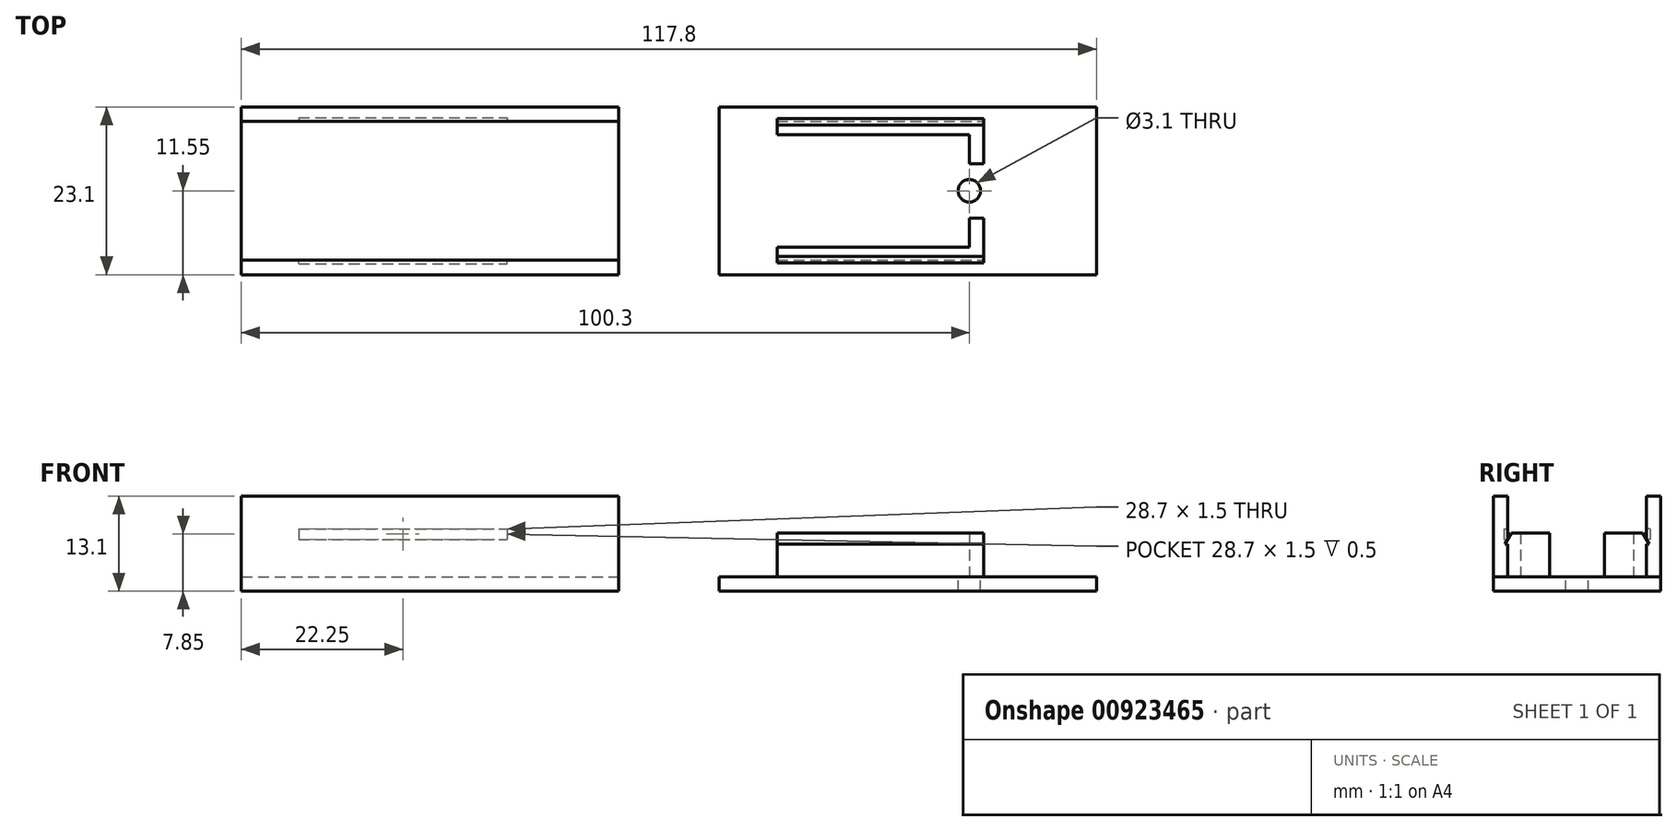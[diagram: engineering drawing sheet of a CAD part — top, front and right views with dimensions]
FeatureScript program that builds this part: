
annotation { "Feature Type Name" : "Feature", "Feature Type Description" : "" }
export const myFeature = defineFeature(function(context is Context, id is Id, definition is map)
    precondition{}
    {
        {
            var Q0;
            Q0=qCreatedBy(makeId("Top.planeOp"),FACE);
            var sketch = newSketch(context, id + "F0", { "sketchPlane" : qUnion([Q0])});
            skLineSegment(sketch, "E0.bottom", {"start": v(-26, 11.55) * mm, "end": v(26, 11.55) * mm});
            skLineSegment(sketch, "E0.top", {"start": v(-26, -11.55) * mm, "end": v(26, -11.55) * mm});
            skLineSegment(sketch, "E0.left", {"start": v(-26, 11.55) * mm, "end": v(-26, -11.55) * mm});
            skLineSegment(sketch, "E0.right", {"start": v(26, 11.55) * mm, "end": v(26, -11.55) * mm});
            skSolve(sketch);
        }
        {
            var Q0;
            Q0 = qSketchRegion(id + "F0", true);
            extrude(context, id + "F1", {"entities" : qUnion([Q0]), "depth" : 2 * mm, "offsetDistance" : 25 * mm});
        }
        {
            var Q0;
            Q0=makeQuery(id+"F1.opExtrude","SWEPT_BODY",BODY,{"disambiguationData":[OSD([sQuery(id+"F0.wireOp",EDGE,"E0.bottom"),sQuery(id+"F0.wireOp",EDGE,"E0.top"),sQuery(id+"F0.wireOp",EDGE,"E0.left"),sQuery(id+"F0.wireOp",EDGE,"E0.right")])]});
            transform(context, id + "F2", {"entities" : qUnion([Q0]), "transformType" : TransformType.TRANSLATION_3D, "dx" : 65.8 * mm, "dy" : 0 * mm, "dz" : 0 * mm, "makeCopy" : true});
        }
        {
            var Q0;
            Q0=makeQuery(id+"F1.opExtrude","CAP_FACE",FACE,{"disambiguationData":[OSD([sQuery(id+"F0.wireOp",EDGE,"E0.bottom"),sQuery(id+"F0.wireOp",EDGE,"E0.top"),sQuery(id+"F0.wireOp",EDGE,"E0.left"),sQuery(id+"F0.wireOp",EDGE,"E0.right")])],"isStart":false});
            var sketch = newSketch(context, id + "F3", { "sketchPlane" : qUnion([Q0])});
            skLineSegment(sketch, "E1.bottom", {"start": v(-26, -11.55) * mm, "end": v(26, -11.55) * mm});
            skLineSegment(sketch, "E1.top", {"start": v(-26, -9.55) * mm, "end": v(26, -9.55) * mm});
            skLineSegment(sketch, "E1.left", {"start": v(-26, -11.55) * mm, "end": v(-26, -9.55) * mm});
            skLineSegment(sketch, "E1.right", {"start": v(26, -11.55) * mm, "end": v(26, -9.55) * mm});
            skLineSegment(sketch, "E2.bottom", {"start": v(-26, 11.55) * mm, "end": v(26, 11.55) * mm});
            skLineSegment(sketch, "E2.top", {"start": v(-26, 9.55) * mm, "end": v(26, 9.55) * mm});
            skLineSegment(sketch, "E2.left", {"start": v(-26, 11.55) * mm, "end": v(-26, 9.55) * mm});
            skLineSegment(sketch, "E2.right", {"start": v(26, 11.55) * mm, "end": v(26, 9.55) * mm});
            skSolve(sketch);
        }
        {
            var Q0;
            Q0 = qSketchRegion(id + "F3", true);
            extrude(context, id + "F4", {"entities" : qUnion([Q0]), "operationType" : NewBodyOperationType.ADD, "depth" : 11.1 * mm, "offsetDistance" : 25 * mm});
        }
        {
            var Q0;
            Q0=makeQuery(id+"F2.opPattern","COPY",FACE,{"derivedFrom":makeQuery(id+"F1.opExtrude","CAP_FACE",FACE,{"disambiguationData":[OSD([sQuery(id+"F0.wireOp",EDGE,"E0.bottom"),sQuery(id+"F0.wireOp",EDGE,"E0.top"),sQuery(id+"F0.wireOp",EDGE,"E0.left"),sQuery(id+"F0.wireOp",EDGE,"E0.right")])],"isStart":false}),"instanceName":"1"});
            var sketch = newSketch(context, id + "F5", { "sketchPlane" : qUnion([Q0])});
            skLineSegment(sketch, "E3.bottom", {"start": v(47.8, -7.75) * mm, "end": v(76.3, -7.75) * mm});
            skLineSegment(sketch, "E3.top", {"start": v(47.8, -9.55) * mm, "end": v(76.3, -9.55) * mm});
            skLineSegment(sketch, "E3.left", {"start": v(47.8, -7.75) * mm, "end": v(47.8, -9.55) * mm});
            skLineSegment(sketch, "E3.right", {"start": v(76.3, -7.75) * mm, "end": v(76.3, -9.55) * mm});
            skLineSegment(sketch, "E4.bottom", {"start": v(47.8, 9.55) * mm, "end": v(76.3, 9.55) * mm});
            skLineSegment(sketch, "E4.top", {"start": v(47.8, 7.75) * mm, "end": v(76.3, 7.75) * mm});
            skLineSegment(sketch, "E4.left", {"start": v(47.8, 9.55) * mm, "end": v(47.8, 7.75) * mm});
            skLineSegment(sketch, "E4.right", {"start": v(76.3, 9.55) * mm, "end": v(76.3, 7.75) * mm});
            skSolve(sketch);
        }
        {
            var Q0;
            Q0 = qSketchRegion(id + "F5", true);
            extrude(context, id + "F6", {"entities" : qUnion([Q0]), "operationType" : NewBodyOperationType.ADD, "depth" : 6 * mm, "offsetDistance" : 25 * mm});
        }
        {
            var Q0;
            Q0=makeQuery(id+"F6.opExtrude","SWEPT_FACE",FACE,{"disambiguationData":[OSD([sQuery(id+"F5.wireOp",EDGE,"E3.top")])]});
            var sketch = newSketch(context, id + "F7", { "sketchPlane" : qUnion([Q0])});
            skLineSegment(sketch, "E5.bottom", {"start": v(47.8, 8) * mm, "end": v(76.3, 8) * mm});
            skLineSegment(sketch, "E5.top", {"start": v(47.8, 6.5) * mm, "end": v(76.3, 6.5) * mm});
            skLineSegment(sketch, "E5.left", {"start": v(47.8, 8) * mm, "end": v(47.8, 6.5) * mm});
            skLineSegment(sketch, "E5.right", {"start": v(76.3, 8) * mm, "end": v(76.3, 6.5) * mm});
            skSolve(sketch);
        }
        {
            var Q0;
            Q0 = qSketchRegion(id + "F7", true);
            extrude(context, id + "F8", {"entities" : qUnion([Q0]), "operationType" : NewBodyOperationType.ADD, "depth" : .5 * mm, "offsetDistance" : 25 * mm});
        }
        {
            var Q0;
            Q0=makeQuery(id+"F8.opExtrude","CAP_EDGE",EDGE,{"disambiguationData":[OSD([sQuery(id+"F7.wireOp",EDGE,"E5.bottom")])],"isStart":false});
            chamfer(context, id + "F9", {"entities" : qUnion([Q0]), "chamferType" : ChamferType.OFFSET_ANGLE, "width" : 1 * mm, "oppositeDirection" : false, "angle" : 60 * degree, "tangentPropagation" : true});
        }
        {
            var Q0;
            Q0=makeQuery(id+"F6.opExtrude","SWEPT_FACE",FACE,{"disambiguationData":[OSD([sQuery(id+"F5.wireOp",EDGE,"E4.bottom")])]});
            var sketch = newSketch(context, id + "F10", { "sketchPlane" : qUnion([Q0])});
            skLineSegment(sketch, "E6.bottom", {"start": v(-76.3, 8) * mm, "end": v(-47.8, 8) * mm});
            skLineSegment(sketch, "E6.top", {"start": v(-76.3, 6.5) * mm, "end": v(-47.8, 6.5) * mm});
            skLineSegment(sketch, "E6.left", {"start": v(-76.3, 8) * mm, "end": v(-76.3, 6.5) * mm});
            skLineSegment(sketch, "E6.right", {"start": v(-47.8, 8) * mm, "end": v(-47.8, 6.5) * mm});
            skSolve(sketch);
        }
        {
            var Q0;
            Q0 = qSketchRegion(id + "F10", true);
            extrude(context, id + "F11", {"entities" : qUnion([Q0]), "operationType" : NewBodyOperationType.ADD, "depth" : .5 * mm, "offsetDistance" : 25 * mm});
        }
        {
            var Q0;
            Q0=makeQuery(id+"F11.opExtrude","CAP_EDGE",EDGE,{"disambiguationData":[OSD([sQuery(id+"F10.wireOp",EDGE,"E6.bottom")])],"isStart":false});
            chamfer(context, id + "F12", {"entities" : qUnion([Q0]), "chamferType" : ChamferType.OFFSET_ANGLE, "width" : 1 * mm, "oppositeDirection" : true, "angle" : 60 * degree, "tangentPropagation" : true});
        }
        {
            var Q0;
            Q0=makeQuery(id+"F4.opExtrude","SWEPT_FACE",FACE,{"disambiguationData":[OSD([sQuery(id+"F3.wireOp",EDGE,"E1.top")])]});
            var sketch = newSketch(context, id + "F13", { "sketchPlane" : qUnion([Q0])});
            skLineSegment(sketch, "E7.bottom", {"start": v(18.1, 8.6) * mm, "end": v(-10.6, 8.6) * mm});
            skLineSegment(sketch, "E7.top", {"start": v(18.1, 7.1) * mm, "end": v(-10.6, 7.1) * mm});
            skLineSegment(sketch, "E7.left", {"start": v(18.1, 8.6) * mm, "end": v(18.1, 7.1) * mm});
            skLineSegment(sketch, "E7.right", {"start": v(-10.6, 8.6) * mm, "end": v(-10.6, 7.1) * mm});
            skSolve(sketch);
        }
        {
            var Q0;
            Q0 = qSketchRegion(id + "F13", true);
            extrude(context, id + "F14", {"entities" : qUnion([Q0]), "operationType" : NewBodyOperationType.REMOVE, "oppositeDirection" : true, "depth" : .5 * mm, "offsetDistance" : 25 * mm});
        }
        {
            var Q0;
            Q0=makeQuery(id+"F4.opExtrude","SWEPT_FACE",FACE,{"disambiguationData":[OSD([sQuery(id+"F3.wireOp",EDGE,"E2.top")])]});
            var sketch = newSketch(context, id + "F15", { "sketchPlane" : qUnion([Q0])});
            skLineSegment(sketch, "E8.bottom", {"start": v(-18.1, 8.6) * mm, "end": v(10.6, 8.6) * mm});
            skLineSegment(sketch, "E8.top", {"start": v(-18.1, 7.1) * mm, "end": v(10.6, 7.1) * mm});
            skLineSegment(sketch, "E8.left", {"start": v(-18.1, 8.6) * mm, "end": v(-18.1, 7.1) * mm});
            skLineSegment(sketch, "E8.right", {"start": v(10.6, 8.6) * mm, "end": v(10.6, 7.1) * mm});
            skSolve(sketch);
        }
        {
            var Q0;
            Q0 = qSketchRegion(id + "F15", true);
            extrude(context, id + "F16", {"entities" : qUnion([Q0]), "operationType" : NewBodyOperationType.REMOVE, "oppositeDirection" : true, "depth" : .5 * mm, "offsetDistance" : 25 * mm});
        }
        {
            var Q0;
            Q0=makeQuery(id+"F2.opPattern","COPY",FACE,{"derivedFrom":makeQuery(id+"F1.opExtrude","CAP_FACE",FACE,{"disambiguationData":[OSD([sQuery(id+"F0.wireOp",EDGE,"E0.bottom"),sQuery(id+"F0.wireOp",EDGE,"E0.top"),sQuery(id+"F0.wireOp",EDGE,"E0.left"),sQuery(id+"F0.wireOp",EDGE,"E0.right")])],"isStart":false}),"instanceName":"1"});
            var sketch = newSketch(context, id + "F17", { "sketchPlane" : qUnion([Q0])});
            skCircle(sketch, "E9", {"center": v(74.3, 0) * mm, "radius": 1.55 * mm});
            skPoint(sketch, "E9.centerSnap0", {"position": v(39.8, 0) * mm});
            skSolve(sketch);
        }
        {
            var Q0;
            Q0 = qSketchRegion(id + "F17", true);
            extrude(context, id + "F18", {"entities" : qUnion([Q0]), "operationType" : NewBodyOperationType.REMOVE, "endBound" : BoundingType.THROUGH_ALL, "oppositeDirection" : true, "depth" : 25 * mm, "offsetDistance" : 25 * mm});
        }
        {
            var Q0;
            Q0=makeQuery(id+"F2.opPattern","COPY",FACE,{"derivedFrom":makeQuery(id+"F1.opExtrude","CAP_FACE",FACE,{"disambiguationData":[OSD([sQuery(id+"F0.wireOp",EDGE,"E0.bottom"),sQuery(id+"F0.wireOp",EDGE,"E0.top"),sQuery(id+"F0.wireOp",EDGE,"E0.left"),sQuery(id+"F0.wireOp",EDGE,"E0.right")])],"isStart":false}),"instanceName":"1"});
            var sketch = newSketch(context, id + "F19", { "sketchPlane" : qUnion([Q0])});
            skLineSegment(sketch, "E10.bottom", {"start": v(76.3, -7.75) * mm, "end": v(74.3, -7.75) * mm});
            skLineSegment(sketch, "E10.top", {"start": v(76.3, -3.75) * mm, "end": v(74.3, -3.75) * mm});
            skLineSegment(sketch, "E10.left", {"start": v(76.3, -7.75) * mm, "end": v(76.3, -3.75) * mm});
            skLineSegment(sketch, "E10.right", {"start": v(74.3, -7.75) * mm, "end": v(74.3, -3.75) * mm});
            skLineSegment(sketch, "E11.bottom", {"start": v(76.3, 7.75) * mm, "end": v(74.3, 7.75) * mm});
            skLineSegment(sketch, "E11.top", {"start": v(76.3, 3.75) * mm, "end": v(74.3, 3.75) * mm});
            skLineSegment(sketch, "E11.left", {"start": v(76.3, 7.75) * mm, "end": v(76.3, 3.75) * mm});
            skLineSegment(sketch, "E11.right", {"start": v(74.3, 7.75) * mm, "end": v(74.3, 3.75) * mm});
            skSolve(sketch);
        }
        {
            var Q0;
            Q0 = qSketchRegion(id + "F19", true);
            extrude(context, id + "F20", {"entities" : qUnion([Q0]), "operationType" : NewBodyOperationType.ADD, "depth" : 6 * mm, "offsetDistance" : 25 * mm});
        }
    });
